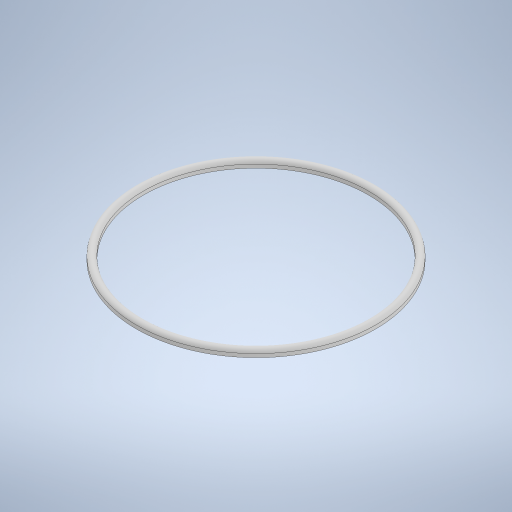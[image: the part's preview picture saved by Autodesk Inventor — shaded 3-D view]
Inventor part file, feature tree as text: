
AUTODESK INVENTOR PART (.ipt)
format: ipt  version: 2023 (Build 270158030, 158C)  size: 259,584 bytes
history: native  units: in
note: dims shown in document units (in); Inventor stores cm internally (conversion verified against a paired STEP export)
features: revolve x1, sketch x1
ambient origin geometry x8: Origin, YZ Plane, XZ Plane, XY Plane, X Axis, Y Axis, Z Axis, Center Point
bodies: Solid1 (feature_tree)
feature tree (2):
  revolve  "Revolution1"  [1 undecoded]
  sketch  "Sketch1"  dims[d0=0.125in d1=4.1339in d3=0.125in d4=90.0deg]
note: 1 required parameter value undecoded (feature->parameter linkage not recoverable at this tier; creation-order binding heuristic only, values carry confidence <= 0.55)
